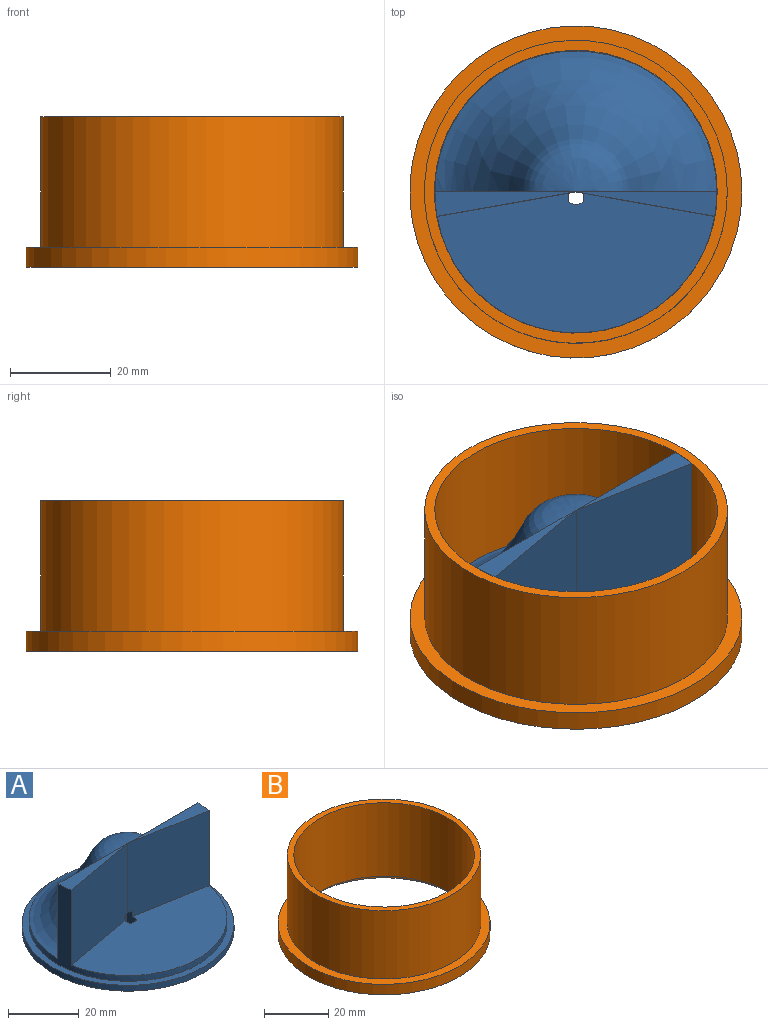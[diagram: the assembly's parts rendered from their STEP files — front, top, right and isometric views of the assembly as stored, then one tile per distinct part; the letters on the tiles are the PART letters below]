
ASSEMBLY  parts=2 mates=1
PART A: 17 faces, bbox 60x60x30 mm
  f0: plane 27.57x26mm, normal (-0.17,-0.98,0), area 725mm2, adj f4,f8,f9,f11,f15,f16
  f1: plane 60x60mm, normal (0,0,-1), area 2813.9mm2, adj f2,f12,f13,f14,f15
  f2: cylinder r=30mm len=60mm, axis (0,0,-1), area 377mm2, adj f1,f3
  f3: plane 60x60mm, normal (0,0,1), area 364.4mm2, adj f2,f4
  f4: cylinder r=28mm len=56mm, axis (0,0,-1), area 606mm2, adj f0,f3,f5,f6,f7,f8,f9,f10
  f5: revolved ~56x28mm, area 1826.2mm2, adj f4,f6,f10
  f6: plane 28x26mm, normal (0,1,0), area 327.1mm2, adj f4,f5,f7
  f7: plane 28x4.86mm, normal (0,0,1), area 68.4mm2, adj f4,f6,f8
  f8: plane 27.57x26mm, normal (0.17,-0.98,0), area 725mm2, adj f0,f4,f7,f11,f13,f16
  f9: plane 28x4.86mm, normal (0,0,1), area 68.4mm2, adj f0,f4,f10
  f10: plane 28x26mm, normal (0,1,0), area 327.1mm2, adj f4,f5,f9
  f11: plane 55.15x27.74mm, normal (0,0,1), area 1088.3mm2, adj f0,f4,f8,f12,f13,f15
  f12: cylinder r=2.45mm len=4mm, axis (0,0,-1), area 12.6mm2, adj f1,f11,f13,f15
  f13: plane 6x3.92mm, normal (1,0,0), area 20.1mm2, adj f1,f8,f11,f12,f14,f16
  f14: cylinder r=2.45mm len=6mm, axis (0,0,-1), area 18.9mm2, adj f1,f13,f15,f16
  f15: plane 6x3.92mm, normal (-1,0,0), area 20.1mm2, adj f0,f1,f11,f12,f14,f16
  f16: plane 2.94x2.71mm, normal (0,0,-1), area 7.1mm2, adj f0,f8,f13,f14,f15
PART B: 8 faces, bbox 66x66x30 mm
  f0: cylinder r=30.1mm len=60.2mm, axis (0,0,-1), area 378.2mm2, adj f3,f5
  f1: cylinder r=33mm len=66mm, axis (0,0,-1), area 829.4mm2, adj f2,f3
  f2: plane 66x66mm, normal (0,0,1), area 574.9mm2, adj f1,f6
  f3: plane 66x66mm, normal (0,0,-1), area 574.9mm2, adj f0,f1
  f4: cylinder r=28.1mm len=56.2mm, axis (0,0,-1), area 4943.6mm2, adj f5,f7
  f5: plane 60.2x60.2mm, normal (0,0,-1), area 365.7mm2, adj f0,f4
  f6: cylinder r=30.1mm len=60.2mm, axis (0,0,-1), area 4917.2mm2, adj f2,f7
  f7: plane 60.2x60.2mm, normal (0,0,1), area 365.7mm2, adj f4,f6
PLACE A t=(-5.41,18.28,-8.68)mm
PLACE B t=(-5.41,18.28,-8.68)mm
MATE fastened B.f1 <-> A.f2  axis (0,0,1) through (-5.41,18.28,-8.68)mm
